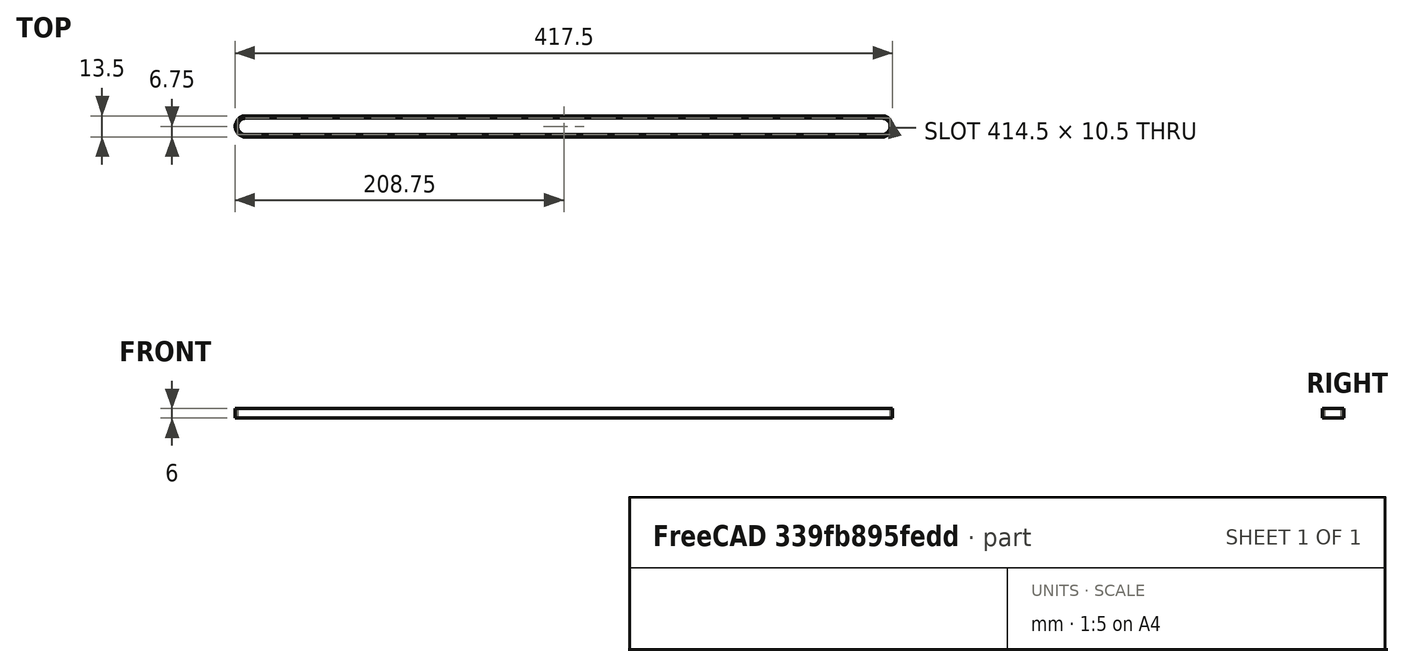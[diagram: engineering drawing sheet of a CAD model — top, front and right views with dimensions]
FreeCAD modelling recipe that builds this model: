
FCSTD DOCUMENT  (FreeCAD 0.14R3310 (Git))
Label: 58. CORREA EJE X GT2 (SIN DIENTES)
License: CC-BY 3.0
LicenseURL: http://creativecommons.org/licenses/by/3.0/
objects: Sketcher::SketchObject×1, PartDesign::Pad×1
note: 3 computed .brp shape members not serialized (recipe doc carries the construction recipe); baked Part::Feature solids carry a one-line shape summary decoded from their .brp

FEATURE [Sketcher::SketchObject] Sketch
  sketch-geometry (8):
    g0: LineSegment StartX=-202 StartY=5.25 StartZ=0 EndX=202 EndY=5.25 EndZ=0
    g1: ArcOfCircle CenterX=202 CenterY=0 CenterZ=0 NormalX=0 NormalY=0 NormalZ=1 Radius=5.25 StartAngle=4.71239 EndAngle=7.85398
    g2: LineSegment StartX=202 StartY=-5.25 StartZ=0 EndX=-202 EndY=-5.25 EndZ=0
    g3: ArcOfCircle CenterX=-202 CenterY=0 CenterZ=0 NormalX=0 NormalY=0 NormalZ=1 Radius=5.25 StartAngle=1.57079 EndAngle=4.71239
    g4: ArcOfCircle CenterX=-202 CenterY=0 CenterZ=0 NormalX=0 NormalY=0 NormalZ=1 Radius=6.75 StartAngle=1.5708 EndAngle=4.71239
    g5: LineSegment StartX=-202 StartY=6.75 StartZ=0 EndX=202 EndY=6.75 EndZ=0
    g6: LineSegment StartX=-202 StartY=-6.75 StartZ=0 EndX=202 EndY=-6.75 EndZ=0
    g7: ArcOfCircle CenterX=202 CenterY=0 CenterZ=0 NormalX=0 NormalY=0 NormalZ=1 Radius=6.75 StartAngle=4.71239 EndAngle=7.85398
  constraints (26):
    c: Distance(g0) = 404
    c: Symmetric(g0,g0,g-2)
    c: PointOnObject(g1,g-1)
    c: Coincident(g1,g0)
    c: Tangent(g1,g0)
    c: Radius(g1) = 5.25
    c: Coincident(g2,g1)
    c: Horizontal(g2)
    c: Equal(g2,g0)
    c: Tangent(g2,g1)
    c: PointOnObject(g3,g-1)
    c: Coincident(g3,g0)
    c: Coincident(g3,g2)
    c: Coincident(g4,g3)
    c: Coincident(g5,g4)
    c: Horizontal(g5)
    c: Tangent(g5,g4)
    c: Radius(g4) = 6.75
    c: Equal(g5,g0)
    c: Coincident(g6,g4)
    c: Horizontal(g6)
    c: Equal(g6,g5)
    c: Tangent(g6,g4)
    c: Coincident(g7,g1)
    c: Coincident(g7,g5)
    c: Coincident(g7,g6)
FEATURE [PartDesign::Pad] Pad
  Length = 6
  Length2 = 100
  Sketch = -> Sketch
  Type = 0
